# Revit family: ONRBH -  1-6-Door - All
name_source: partatom
category: Mechanical Equipment
revit_build: Autodesk Revit 2017 (Build: 20181011_1645(x64)
units: mm (PartAtom-declared; Revit-internal decimal feet)

## family parameters
Always vertical = Yes
Cut with Voids When Loaded = No
OmniClass Number = 23.40.40.11.17
OmniClass Title = Refrigerated Cases
Part Type = Normal
Room Calculation Point = No
Round Connector Dimension = Use Radius
Shared = No
Work Plane-Based = Yes

## types (10) — shared parameters
22" Shelf = Yes
Application Discipline = Beverage
Certifications = NSF 7, UL471, CSA
DATE = 12/21/2015
Default Elevation = 48"
Defrosts Per Day_2 = 4
Description = High Narrow Reach-In Merchandiser
Discharge Air (°F) = 38 °F
Discharge Air Velocity (FPM) = 380 (FPM)
EQUIPMENT DESCRIPTION = High Narrow Reach-In Merchandiser
EQUIPMENT MARK = ONRBH
Evaporator (°F) = 34 °F
Height = 68"
Item Description = High Narrow Reach-In Merchandiser
Keynote = ONRBH
Legend Number = ONRBH
Manufacturer = HILL PHOENIX
Model = ONRBH
Size of Door = 30"
Superheat Set Point @ Bulb (°F) = 6-8 °F
TRIM = BLACK PAINTED METAL
Timed-Off Defrost Fail-Safe (Min) = 30 (Min)
Timed-Off Defrost Termination Temp_2 = 47 °F
Type of Door Swing = A-Swing
URL = http://www.hillphoenix.com
Width = 34 5/8"

## per-type parameters (varying)
- 1-Door- Beverage: 101 Amps=0 A; 101 Watts=28 W; 20" Shelf=No; BTUH Conventional=549; BTUH Parallel=519; CENTER LINE & DRAIN=15 1/2"; Crossfire/Polaris Amps=0 A; Crossfire/Polaris Watts=15 W; DOOR CONFIGURATION=MASTER DOOR : 31" X 68 3/8" 1 DOOR A SWING (LEFT OPENING); Eliminaator Amps=0 A; Eliminaator Watts=28 W; FAN QUANTITY=1; GE Immersion Amps=0 A; GE Immersion Watts=16 W; High Efficiency Amps=0 A; High Efficiency Watts=26 W; How Many Fans Per Case=1; Length=31"; Number of Doors=1; Optimax Pro Amps=0 A; Optimax Pro Watts=20 W; Vista Optimax Pro Amps=0 A; Vista Optimax Pro Watts=20 W; Vista-C/60 Amps=0 A; Vista-C/60 Watts=34 W
- 2-Door- Beverage: 101 Amps=0 A; 101 Watts=47 W; 20" Shelf=No; BTUH Conventional=597; BTUH Parallel=564; CENTER LINE & DRAIN=30"; Crossfire/Polaris Amps=0 A; Crossfire/Polaris Watts=30 W; DOOR CONFIGURATION=MASTER DOOR : 30" X 68 3/8" 2 DOOR A SWING (LEFT OPENING); Eliminaator Amps=0 A; Eliminaator Watts=47 W; FAN QUANTITY=2; GE Immersion Amps=0 A; GE Immersion Watts=32 W; High Efficiency Amps=0 A; High Efficiency Watts=53 W; How Many Fans Per Case=1; Length=60"; Number of Doors=2; Optimax Pro Amps=0 A; Optimax Pro Watts=39 W; Vista Optimax Pro Amps=0 A; Vista Optimax Pro Watts=39 W; Vista-C/60 Amps=1 A; Vista-C/60 Watts=68 W
- 3-Door- Beverage: 101 Amps=1 A; 101 Watts=68 W; 20" Shelf=Yes; BTUH Conventional=597; BTUH Parallel=564; CENTER LINE & DRAIN=45"; Crossfire/Polaris Amps=0 A; Crossfire/Polaris Watts=45 W; DOOR CONFIGURATION=MASTER DOOR : 30" X 68 3/8" 3 DOOR A SWING (LEFT OPENING); Eliminaator Amps=1 A; Eliminaator Watts=68 W; FAN QUANTITY=3; GE Immersion Amps=0 A; GE Immersion Watts=48 W; High Efficiency Amps=1 A; High Efficiency Watts=79 W; How Many Fans Per Case=2; Length=90"; Number of Doors=3; Optimax Pro Amps=0 A; Optimax Pro Watts=58 W; Vista Optimax Pro Amps=0 A; Vista Optimax Pro Watts=58 W; Vista-C/60 Amps=1 A; Vista-C/60 Watts=91 W
- 4-Door- Beverage: 101 Amps=1 A; 101 Watts=91 W; 20" Shelf=Yes; BTUH Conventional=597; BTUH Parallel=564; CENTER LINE & DRAIN=60"; Crossfire/Polaris Amps=1 A; Crossfire/Polaris Watts=60 W; DOOR CONFIGURATION=MASTER DOOR : 30" X 68 3/8" 4 DOOR A SWING (LEFT OPENING); Eliminaator Amps=1 A; Eliminaator Watts=91 W; FAN QUANTITY=4; GE Immersion Amps=1 A; GE Immersion Watts=64 W; High Efficiency Amps=1 A; High Efficiency Watts=106 W; How Many Fans Per Case=2; Length=120"; Number of Doors=1; Optimax Pro Amps=1 A; Optimax Pro Watts=77 W; Vista Optimax Pro Amps=1 A; Vista Optimax Pro Watts=77 W; Vista-C/60 Amps=1 A; Vista-C/60 Watts=111 W
- 5-Door- Beverage: 101 Amps=1 A; 101 Watts=111 W; 20" Shelf=Yes; BTUH Conventional=44; BTUH Parallel=564; CENTER LINE & DRAIN=75"; Crossfire/Polaris Amps=1 A; Crossfire/Polaris Watts=75 W; DOOR CONFIGURATION=MASTER DOOR : 30" X 68 3/8" 5 DOOR A SWING (LEFT OPENING); Eliminaator Amps=1 A; Eliminaator Watts=111 W; FAN QUANTITY=5; GE Immersion Amps=1 A; GE Immersion Watts=80 W; High Efficiency Amps=1 A; High Efficiency Watts=132 W; How Many Fans Per Case=3; Length=150"; Number of Doors=5; Optimax Pro Amps=1 A; Optimax Pro Watts=96 W; Vista Optimax Pro Amps=1 A; Vista Optimax Pro Watts=96 W; Vista-C/60 Amps=1 A; Vista-C/60 Watts=134 W
- 6-Door- Beverage: 101 Amps=1 A; 101 Watts=134 W; 20" Shelf=Yes; BTUH Conventional=597; BTUH Parallel=564; CENTER LINE & DRAIN=90"; Crossfire/Polaris Amps=1 A; Crossfire/Polaris Watts=90 W; DOOR CONFIGURATION=MASTER DOOR : 30" X 68 3/8" 6 DOOR A SWING (LEFT OPENING); Eliminaator Amps=1 A; Eliminaator Watts=134 W; FAN QUANTITY=6; GE Immersion Amps=1 A; GE Immersion Watts=96 W; High Efficiency Amps=1 A; High Efficiency Watts=158 W; How Many Fans Per Case=3; Length=180"; Number of Doors=6; Optimax Pro Amps=1 A; Optimax Pro Watts=115 W; Vista Optimax Pro Amps=1 A; Vista Optimax Pro Watts=115 W; Vista-C/60 Amps=1 A; Vista-C/60 Watts=159 W
- 4': 101 Amps=1 A; 101 Watts=134 W; 20" Shelf=Yes; BTUH Conventional=597; BTUH Parallel=564; CENTER LINE & DRAIN=24"; Crossfire/Polaris Amps=1 A; Crossfire/Polaris Watts=90 W; DOOR CONFIGURATION=MASTER DOOR : 4'; Eliminaator Amps=1 A; Eliminaator Watts=134 W; FAN QUANTITY=6; GE Immersion Amps=1 A; GE Immersion Watts=96 W; High Efficiency Amps=1 A; High Efficiency Watts=158 W; How Many Fans Per Case=3; Length=48"; Number of Doors=6; Optimax Pro Amps=1 A; Optimax Pro Watts=115 W; Vista Optimax Pro Amps=1 A; Vista Optimax Pro Watts=115 W; Vista-C/60 Amps=1 A; Vista-C/60 Watts=159 W
- 6': 101 Amps=1 A; 101 Watts=134 W; 20" Shelf=Yes; BTUH Conventional=597; BTUH Parallel=564; CENTER LINE & DRAIN=36"; Crossfire/Polaris Amps=1 A; Crossfire/Polaris Watts=90 W; DOOR CONFIGURATION=MASTER DOOR : 6'; Eliminaator Amps=1 A; Eliminaator Watts=134 W; FAN QUANTITY=6; GE Immersion Amps=1 A; GE Immersion Watts=96 W; High Efficiency Amps=1 A; High Efficiency Watts=158 W; How Many Fans Per Case=3; Length=72"; Number of Doors=6; Optimax Pro Amps=1 A; Optimax Pro Watts=115 W; Vista Optimax Pro Amps=1 A; Vista Optimax Pro Watts=115 W; Vista-C/60 Amps=1 A; Vista-C/60 Watts=159 W
- 8': 101 Amps=1 A; 101 Watts=134 W; 20" Shelf=Yes; BTUH Conventional=597; BTUH Parallel=564; CENTER LINE & DRAIN=48"; Crossfire/Polaris Amps=1 A; Crossfire/Polaris Watts=90 W; DOOR CONFIGURATION=MASTER DOOR : 8'; Eliminaator Amps=1 A; Eliminaator Watts=134 W; FAN QUANTITY=6; GE Immersion Amps=1 A; GE Immersion Watts=96 W; High Efficiency Amps=1 A; High Efficiency Watts=158 W; How Many Fans Per Case=3; Length=96"; Number of Doors=6; Optimax Pro Amps=1 A; Optimax Pro Watts=115 W; Vista Optimax Pro Amps=1 A; Vista Optimax Pro Watts=115 W; Vista-C/60 Amps=1 A; Vista-C/60 Watts=159 W
- 12': 101 Amps=1 A; 101 Watts=134 W; 20" Shelf=Yes; BTUH Conventional=597; BTUH Parallel=564; CENTER LINE & DRAIN=72"; Crossfire/Polaris Amps=1 A; Crossfire/Polaris Watts=90 W; DOOR CONFIGURATION=MASTER DOOR : 12'; Eliminaator Amps=1 A; Eliminaator Watts=134 W; FAN QUANTITY=6; GE Immersion Amps=1 A; GE Immersion Watts=96 W; High Efficiency Amps=1 A; High Efficiency Watts=158 W; How Many Fans Per Case=3; Length=144"; Number of Doors=6; Optimax Pro Amps=1 A; Optimax Pro Watts=115 W; Vista Optimax Pro Amps=1 A; Vista Optimax Pro Watts=115 W; Vista-C/60 Amps=1 A; Vista-C/60 Watts=159 W

## geometry (parser evidence)
native form markers: Blend x6, Sweep x27
no freeform markers — native parametric forms only
